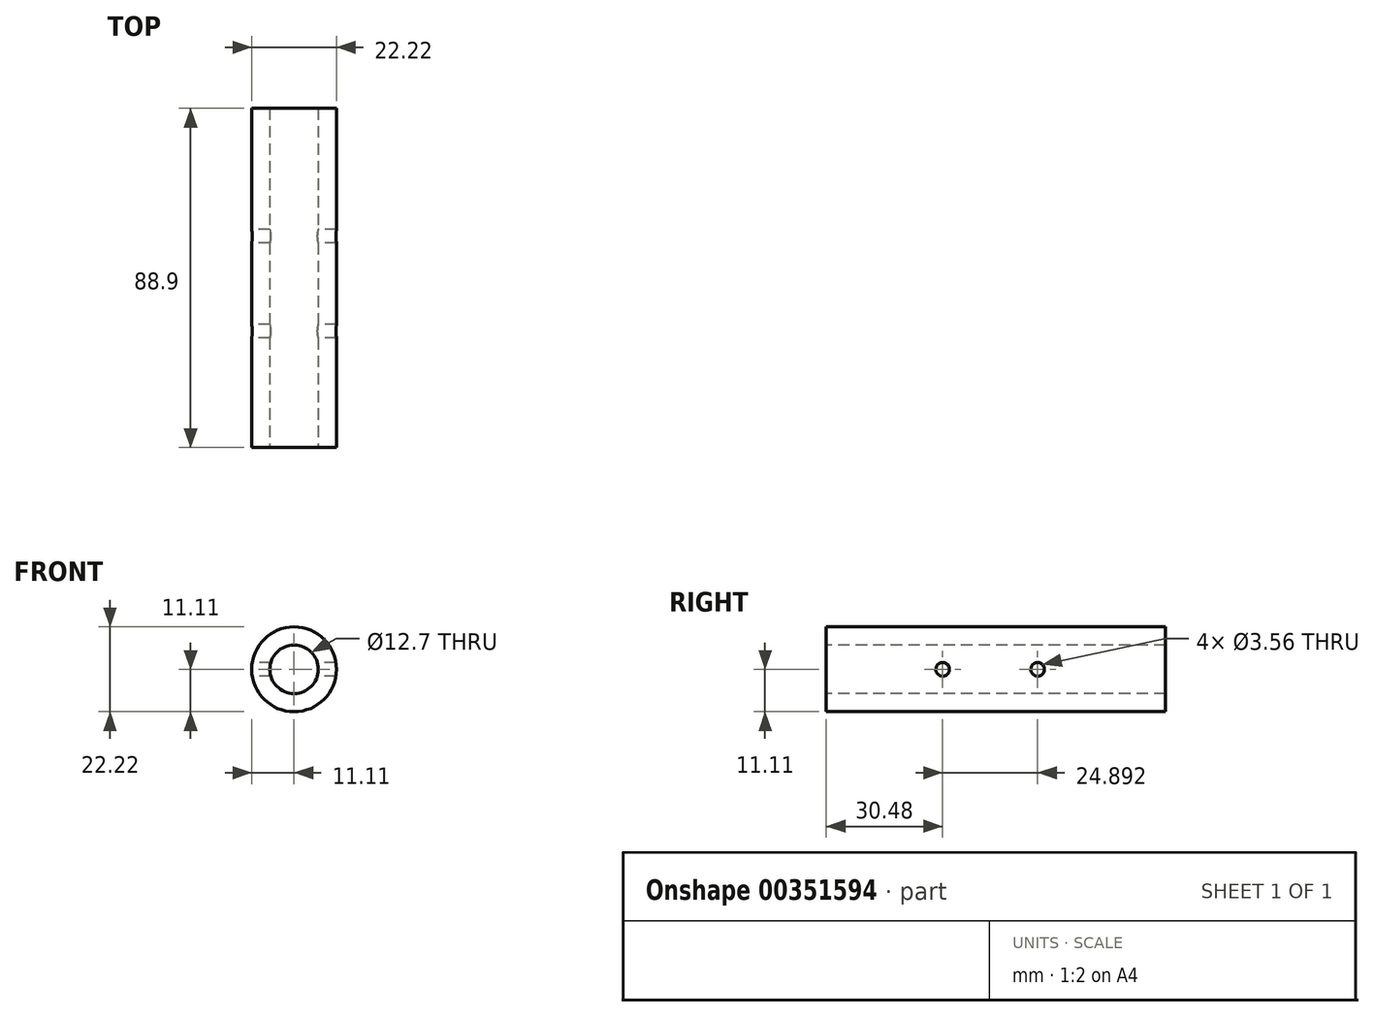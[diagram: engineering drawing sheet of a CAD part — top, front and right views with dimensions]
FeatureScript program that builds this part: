
annotation { "Feature Type Name" : "Feature", "Feature Type Description" : "" }
export const myFeature = defineFeature(function(context is Context, id is Id, definition is map)
    precondition{}
    {
        {
            var Q0;
            Q0=qCreatedBy(makeId("Front.planeOp"),FACE);
            var sketch = newSketch(context, id + "F0", { "sketchPlane" : qUnion([Q0])});
            skCircle(sketch, "E0", {"center": v(0, 0) * mm, "radius": 11.11 * mm});
            skSolve(sketch);
        }
        {
            var Q0;
            Q0 = qSketchRegion(id + "F0", true);
            extrude(context, id + "F1", {"entities" : qUnion([Q0]), "depth" : 88.9 * mm, "symmetric" : true});
        }
        {
            var Q0;
            Q0=makeQuery(id+"F1.opExtrude","CAP_FACE",FACE,{"disambiguationData":[OSD([sQuery(id+"F0.wireOp",EDGE,"E0")])],"isStart":false});
            var sketch = newSketch(context, id + "F2", { "sketchPlane" : qUnion([Q0])});
            skCircle(sketch, "E1", {"center": v(0, 0) * mm, "radius": 6.35 * mm});
            skSolve(sketch);
        }
        {
            var Q0;
            Q0 = qSketchRegion(id + "F2", true);
            var Q1;
            Q1=makeQuery(id+"F1.opExtrude","CAP_FACE",FACE,{"disambiguationData":[OSD([sQuery(id+"F0.wireOp",EDGE,"E0")])],"isStart":true});
            extrude(context, id + "F3", {"entities" : qUnion([Q0]), "operationType" : NewBodyOperationType.REMOVE, "endBound" : BoundingType.UP_TO_SURFACE, "oppositeDirection" : true, "endBoundEntityFace" : qUnion([Q1]), "depth" : 25.4 * mm});
        }
        {
            var Q0;
            Q0=qCreatedBy(makeId("Right.planeOp"),FACE);
            var sketch = newSketch(context, id + "F4", { "sketchPlane" : qUnion([Q0])});
            skCircle(sketch, "E2", {"center": v(-13.97, 0) * mm, "radius": 1.78 * mm});
            skSolve(sketch);
        }
        {
            var Q0;
            Q0 = qSketchRegion(id + "F4", true);
            extrude(context, id + "F5", {"entities" : qUnion([Q0]), "operationType" : NewBodyOperationType.REMOVE, "depth" : 25.4 * mm, "symmetric" : true});
        }
        {
            var Q0;
            Q0=qCreatedBy(makeId("Right.planeOp"),FACE);
            var sketch = newSketch(context, id + "F6", { "sketchPlane" : qUnion([Q0])});
            skCircle(sketch, "E3", {"center": v(10.92, 0) * mm, "radius": 1.78 * mm});
            skSolve(sketch);
        }
        {
            var Q0;
            Q0 = qSketchRegion(id + "F6", true);
            extrude(context, id + "F7", {"entities" : qUnion([Q0]), "operationType" : NewBodyOperationType.REMOVE, "depth" : 25.4 * mm, "symmetric" : true});
        }
    });
